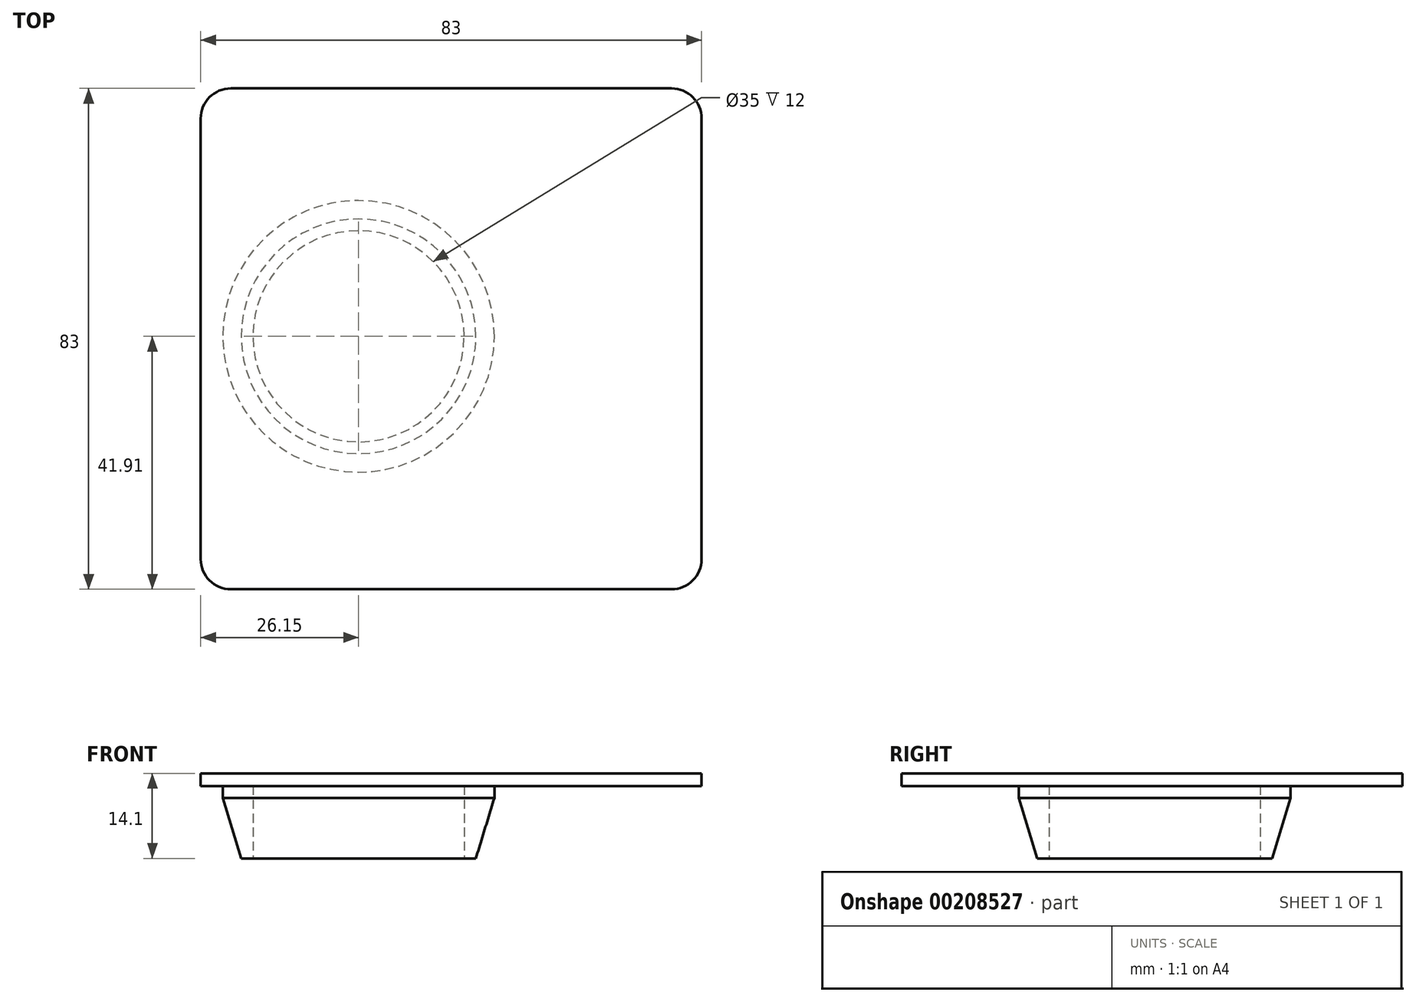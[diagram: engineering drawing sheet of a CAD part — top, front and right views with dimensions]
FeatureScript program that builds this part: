
annotation { "Feature Type Name" : "Feature", "Feature Type Description" : "" }
export const myFeature = defineFeature(function(context is Context, id is Id, definition is map)
    precondition{}
    {
        {
            var Q0;
            Q0=qCreatedBy(makeId("Top.planeOp"),FACE);
            var sketch = newSketch(context, id + "F0", { "sketchPlane" : qUnion([Q0])});
            skCircle(sketch, "E0", {"center": v(0, 0) * mm, "radius": 22.5 * mm});
            skCircle(sketch, "E1", {"center": v(0, 0) * mm, "radius": 17.5 * mm});
            skSolve(sketch);
        }
        {
            var Q0;
            Q0 = qSketchRegion(id + "F0", true);
            var Q1;
            Q1=sQuery(id+"F0.wireOp",EDGE,"E0");
            extrude(context, id + "F1", {"entities" : qUnion([Q0]), "surfaceEntities" : qUnion([Q1]), "depth" : 12 * mm});
        }
        {
            var Q0;
            Q0=makeQuery(id+"F1.opExtrude","CAP_EDGE",EDGE,{"disambiguationData":[OSD([sQuery(id+"F0.wireOp",EDGE,"E0")])],"isStart":true});
            chamfer(context, id + "F2", {"entities" : qUnion([Q0]), "chamferType" : ChamferType.OFFSET_ANGLE, "width" : 10 * mm, "oppositeDirection" : false, "angle" : 17 * degree, "tangentPropagation" : true});
        }
        {
            var Q0;
            Q0=qCreatedBy(makeId("Top.planeOp"),FACE);
            var Q1;
            Q1 = qBodyType(qCreatedBy(id + "F4" ,EDGE), BodyType.WIRE);
            cPlane(context, id + "F3", {"entities" : qUnion([Q0, Q1]), "cplaneType" : CPlaneType.OFFSET, "offset" : 14.1 * mm, "width" : 152.4 * mm, "height" : 152.4 * mm});
        }
        {
            var Q0;
            Q0=qCreatedBy(id+"F3.planeOp",FACE);
            var sketch = newSketch(context, id + "F4", { "sketchPlane" : qUnion([Q0])});
            skLineSegment(sketch, "E2.bottom", {"start": v(-26.15, 41.09) * mm, "end": v(56.85, 41.09) * mm});
            skLineSegment(sketch, "E2.top", {"start": v(-26.15, -41.91) * mm, "end": v(56.85, -41.91) * mm});
            skLineSegment(sketch, "E2.left", {"start": v(-26.15, 41.09) * mm, "end": v(-26.15, -41.91) * mm});
            skLineSegment(sketch, "E2.right", {"start": v(56.85, 41.09) * mm, "end": v(56.85, -41.91) * mm});
            skPoint(sketch, "E2.middle", {"position": v(15.35, -0.41) * mm});
            skSolve(sketch);
        }
        {
            var Q0;
            Q0=makeQuery(id+"F4.imprint","IMPRINT",FACE,{"disambiguationData":[TD([[makeQuery(id+"F4.imprint","IMPRINT",EDGE,{"derivedFrom":sQuery(id+"F4.wireOp",EDGE,"E2.bottom")}),-1.0]])]});
            extrude(context, id + "F5", {"entities" : qUnion([Q0]), "operationType" : NewBodyOperationType.ADD, "oppositeDirection" : true, "depth" : 2.1 * mm});
        }
        {
            var Q0;
            Q0=makeQuery(id+"F5.opExtrude","SWEPT_EDGE",EDGE,{"disambiguationData":[OSD([sQuery(id+"F4.wireOp",EDGE,"E2.top"),sQuery(id+"F4.wireOp",EDGE,"E2.left")])]});
            var Q1;
            Q1=makeQuery(id+"F5.opExtrude","SWEPT_EDGE",EDGE,{"disambiguationData":[OSD([sQuery(id+"F4.wireOp",EDGE,"E2.top"),sQuery(id+"F4.wireOp",EDGE,"E2.right")])]});
            var Q2;
            Q2=makeQuery(id+"F5.opExtrude","SWEPT_EDGE",EDGE,{"disambiguationData":[OSD([sQuery(id+"F4.wireOp",EDGE,"E2.bottom"),sQuery(id+"F4.wireOp",EDGE,"E2.left")])]});
            var Q3;
            Q3=makeQuery(id+"F5.opExtrude","SWEPT_EDGE",EDGE,{"disambiguationData":[OSD([sQuery(id+"F4.wireOp",EDGE,"E2.bottom"),sQuery(id+"F4.wireOp",EDGE,"E2.right")])]});
            fillet(context, id + "F6", {"entities" : qUnion([Q0, Q1, Q2, Q3]), "radius" : 5 * mm, "tangentPropagation" : true, "allowEdgeOverflow" : false});
        }
    });
